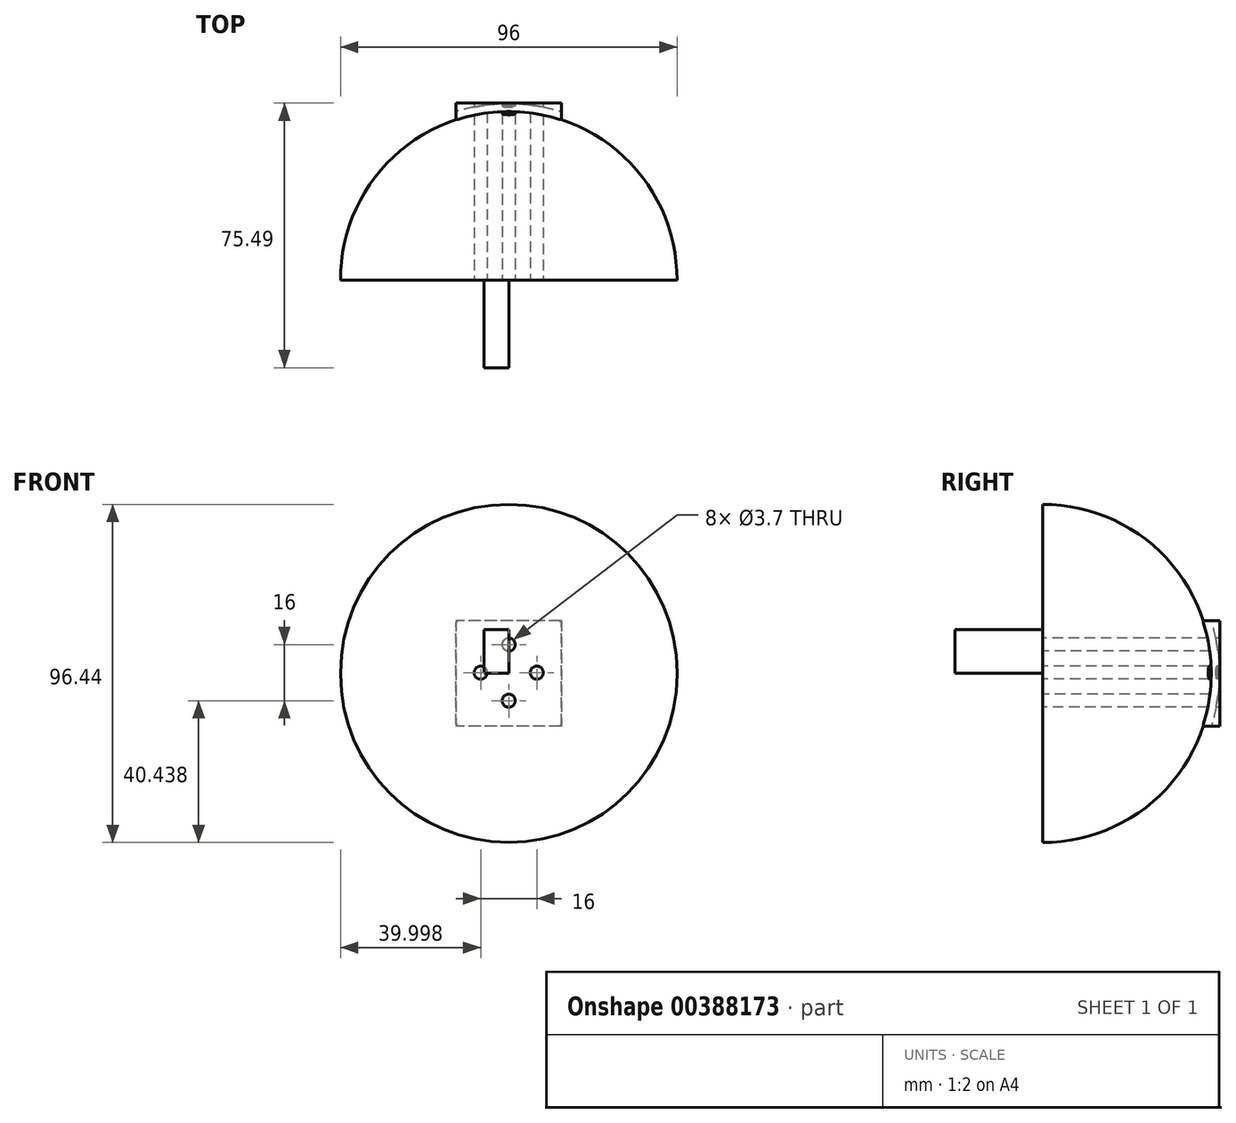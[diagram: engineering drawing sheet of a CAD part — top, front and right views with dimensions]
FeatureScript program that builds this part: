
annotation { "Feature Type Name" : "Feature", "Feature Type Description" : "" }
export const myFeature = defineFeature(function(context is Context, id is Id, definition is map)
    precondition{}
    {
        {
            var Q0;
            Q0=qCreatedBy(makeId("Front.planeOp"),FACE);
            var sketch = newSketch(context, id + "F0", { "sketchPlane" : qUnion([Q0])});
            skArc(sketch, "E0", {"start": v(100.3, 0) * mm, "mid": v(50.15, 50.37) * mm, "end": v(0, 0) * mm});
            skLineSegment(sketch, "E1", {"start": v(0, 0) * mm, "end": v(100.3, 0) * mm});
            skSolve(sketch);
        }
        {
            var Q0;
            Q0=makeQuery(id+"F0.imprint","IMPRINT",FACE,{"disambiguationData":[TD([[makeQuery(id+"F0.imprint","IMPRINT",EDGE,{"derivedFrom":sQuery(id+"F0.wireOp",EDGE,"n1WVY9X2-CB0U-0t6R-Ixkn-eU322xIvqkJW")}),1.0]])]});
            var Q1;
            Q1=makeQuery(id+"F0.imprint","IMPRINT",FACE,{"disambiguationData":[TD([[makeQuery(id+"F0.imprint","IMPRINT",EDGE,{"derivedFrom":sQuery(id+"F0.wireOp",EDGE,"E0")}),1.0]])]});
            var Q2;
            Q2=sQuery(id+"F0.wireOp",EDGE,"E1");
            revolve(context, id + "F1", {"entities" : qUnion([Q0, Q1]), "axis" : qUnion([Q2]), "revolveType" : RevolveType.ONE_DIRECTION, "oppositeDirection" : true, "angle" : 180 * degree});
        }
        {
            var Q0;
            Q0=qCreatedBy(makeId("Front.planeOp"),FACE);
            var sketch = newSketch(context, id + "F2", { "sketchPlane" : qUnion([Q0])});
            skArc(sketch, "E2.0", {"start": v(100.3, 0) * mm, "mid": v(50.15, 50.37) * mm, "end": v(0, 0) * mm});
            skLineSegment(sketch, "E3.0", {"start": v(0, 0) * mm, "end": v(100.3, 0) * mm});
            skArc(sketch, "E4", {"start": v(2.15, 0) * mm, "mid": v(50.15, 48.22) * mm, "end": v(98.15, 0) * mm});
            skLineSegment(sketch, "E5", {"start": v(2.15, 0) * mm, "end": v(98.15, 0) * mm});
            skSolve(sketch);
        }
        {
            var Q0;
            Q0=qCreatedBy(makeId("Front.planeOp"),FACE);
            var sketch = newSketch(context, id + "F3", { "sketchPlane" : qUnion([Q0])});
            skPoint(sketch, "E6.0", {"position": v(50.15, 0) * mm});
            skLineSegment(sketch, "E7.bottom", {"start": v(50.15, 0) * mm, "end": v(43.1, 0) * mm});
            skLineSegment(sketch, "E7.top", {"start": v(50.15, 12.54) * mm, "end": v(43.1, 12.54) * mm});
            skLineSegment(sketch, "E7.left", {"start": v(50.15, 0) * mm, "end": v(50.15, 12.54) * mm});
            skLineSegment(sketch, "E7.right", {"start": v(43.1, 0) * mm, "end": v(43.1, 12.54) * mm});
            skSolve(sketch);
        }
        {
            var Q0;
            Q0=makeQuery(id+"F3.imprint","IMPRINT",FACE,{"disambiguationData":[TD([[makeQuery(id+"F3.imprint","IMPRINT",EDGE,{"derivedFrom":sQuery(id+"F3.wireOp",EDGE,"E7.bottom")}),-1.0]])]});
            extrude(context, id + "F4", {"entities" : qUnion([Q0]), "depth" : 25 * mm});
        }
        {
            var Q0;
            Q0=makeQuery(id+"F4.opExtrude","SWEPT_FACE",FACE,{"disambiguationData":[OSD([sQuery(id+"F3.wireOp",EDGE,"E7.left")])]});
            var sketch = newSketch(context, id + "F5", { "sketchPlane" : qUnion([Q0])});
            skLineSegment(sketch, "E8.bottom", {"start": v(50.5, 15) * mm, "end": v(45.85, 15) * mm});
            skLineSegment(sketch, "E8.top", {"start": v(50.5, -15) * mm, "end": v(45.85, -15) * mm});
            skLineSegment(sketch, "E8.left", {"start": v(50.5, 15) * mm, "end": v(50.5, -15) * mm});
            skLineSegment(sketch, "E8.right", {"start": v(45.85, 15) * mm, "end": v(45.85, -15) * mm});
            skPoint(sketch, "E8.middle", {"position": v(48.17, 0) * mm});
            skSolve(sketch);
        }
        {
            var Q0;
            Q0 = qSketchRegion(id + "F5", true);
            extrude(context, id + "F6", {"entities" : qUnion([Q0]), "operationType" : NewBodyOperationType.ADD, "endBound" : BoundingType.SYMMETRIC, "depth" : 30 * mm});
        }
        {
            var Q0;
            Q0=makeQuery(id+"F2.imprint","IMPRINT",FACE,{"disambiguationData":[TD([[makeQuery(id+"F2.imprint","IMPRINT",EDGE,{"derivedFrom":sQuery(id+"F2.wireOp",EDGE,"E4")}),-1.0]])]});
            var Q1;
            Q1=sQuery(id+"F2.wireOp",EDGE,"E5");
            revolve(context, id + "F7", {"operationType" : NewBodyOperationType.REMOVE, "entities" : qUnion([Q0]), "axis" : qUnion([Q1]), "revolveType" : RevolveType.ONE_DIRECTION, "oppositeDirection" : true, "angle" : 180 * degree});
        }
        {
            var Q0;
            Q0=qCreatedBy(makeId("Front.planeOp"),FACE);
            var sketch = newSketch(context, id + "F8", { "sketchPlane" : qUnion([Q0])});
            skPoint(sketch, "E9.0", {"position": v(50.15, 0.22) * mm});
            skLineSegment(sketch, "E10", {"start": v(50.15, 0.22) * mm, "end": v(42.15, 0.22) * mm});
            skCircle(sketch, "E11", {"center": v(42.15, 0.22) * mm, "radius": 1.85 * mm});
            skLineSegment(sketch, "E12", {"start": v(50.15, 0.22) * mm, "end": v(58.15, 0.22) * mm});
            skCircle(sketch, "E13", {"center": v(58.15, 0.22) * mm, "radius": 1.85 * mm});
            skLineSegment(sketch, "E14", {"start": v(50.15, 0.22) * mm, "end": v(50.15, 8.22) * mm});
            skCircle(sketch, "E15", {"center": v(50.15, 8.22) * mm, "radius": 1.85 * mm});
            skLineSegment(sketch, "E16", {"start": v(50.15, 0.22) * mm, "end": v(50.15, -7.78) * mm});
            skCircle(sketch, "E17", {"center": v(50.15, -7.78) * mm, "radius": 1.85 * mm});
            skSolve(sketch);
        }
        {
            var Q0;
            Q0=makeQuery(id+"F8.imprint","IMPRINT",FACE,{"disambiguationData":[TD([[makeQuery(id+"F8.imprint","IMPRINT",EDGE,{"derivedFrom":sQuery(id+"F8.wireOp",EDGE,"E15")}),1.0]])]});
            var Q1;
            Q1=makeQuery(id+"F8.imprint","IMPRINT",FACE,{"disambiguationData":[TD([[makeQuery(id+"F8.imprint","IMPRINT",EDGE,{"derivedFrom":sQuery(id+"F8.wireOp",EDGE,"E11")}),1.0]])]});
            var Q2;
            Q2=makeQuery(id+"F8.imprint","IMPRINT",FACE,{"disambiguationData":[TD([[makeQuery(id+"F8.imprint","IMPRINT",EDGE,{"derivedFrom":sQuery(id+"F8.wireOp",EDGE,"E13")}),1.0]])]});
            var Q3;
            Q3=makeQuery(id+"F8.imprint","IMPRINT",FACE,{"disambiguationData":[TD([[makeQuery(id+"F8.imprint","IMPRINT",EDGE,{"derivedFrom":sQuery(id+"F8.wireOp",EDGE,"E17")}),1.0]])]});
            extrude(context, id + "F9", {"entities" : qUnion([Q0, Q1, Q2, Q3]), "operationType" : NewBodyOperationType.REMOVE, "oppositeDirection" : true, "depth" : 60 * mm});
        }
    });
